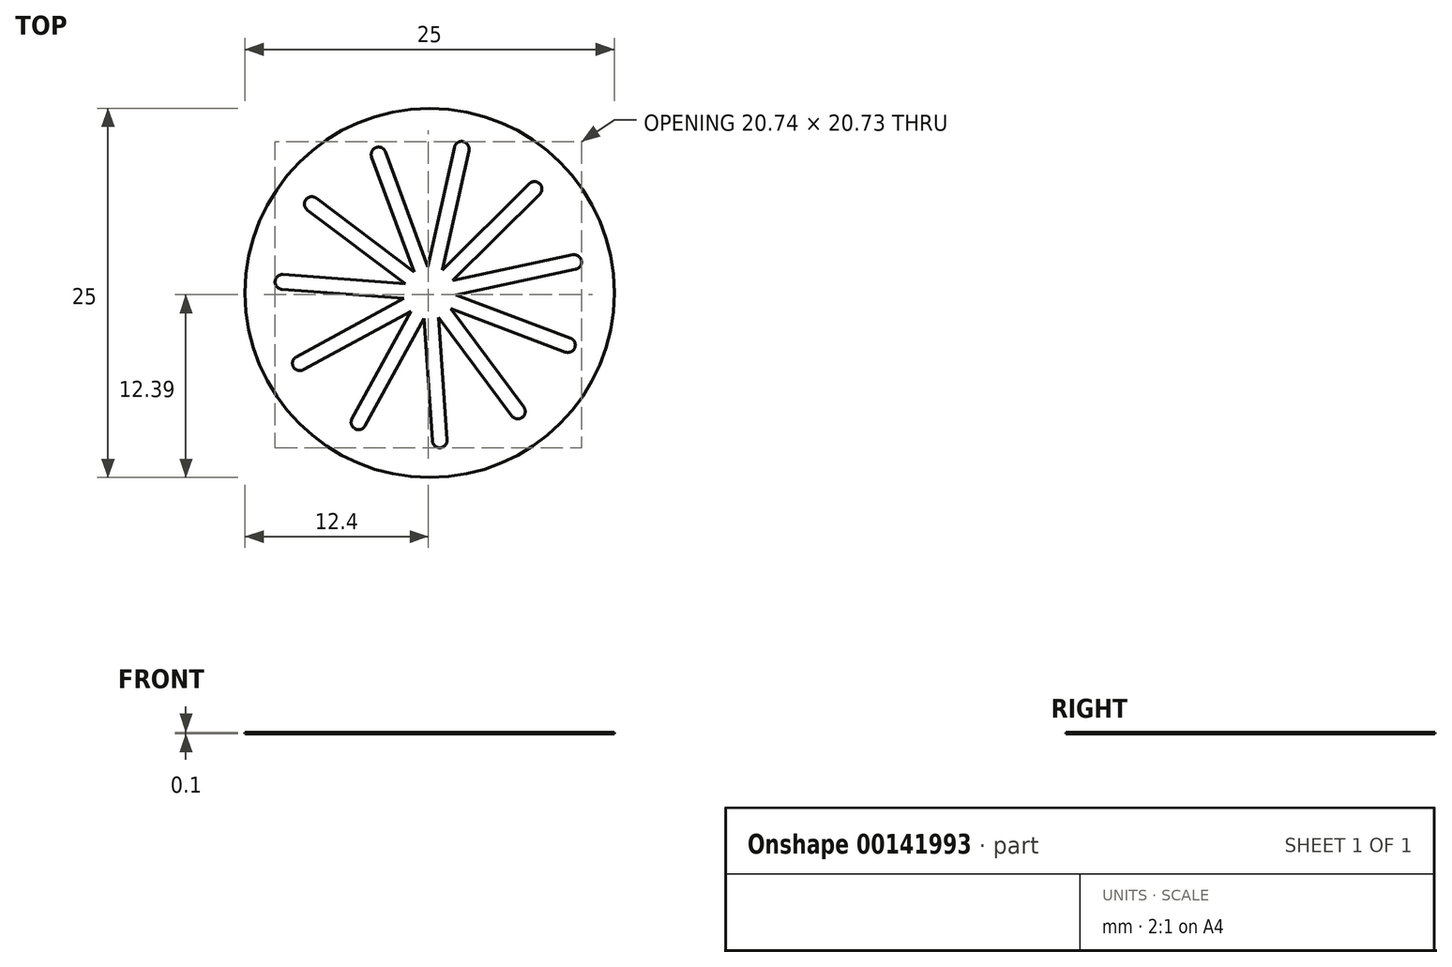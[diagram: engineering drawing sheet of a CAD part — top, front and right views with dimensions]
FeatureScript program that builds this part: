
annotation { "Feature Type Name" : "Feature", "Feature Type Description" : "" }
export const myFeature = defineFeature(function(context is Context, id is Id, definition is map)
    precondition{}
    {
        {
            var Q0;
            Q0=qCreatedBy(makeId("Top.planeOp"),FACE);
            var sketch = newSketch(context, id + "F0", { "sketchPlane" : qUnion([Q0])});
            skLineSegment(sketch, "E0", {"start": v(0.86, 1.55) * mm, "end": v(2.65, 9.66) * mm});
            skLineSegment(sketch, "E1", {"start": v(-0.12, 1.77) * mm, "end": v(1.67, 9.87) * mm});
            skArc(sketch, "E2", {"start": v(2.65, 9.66) * mm, "mid": v(2.27, 10.25) * mm, "end": v(1.67, 9.87) * mm});
            skArc(sketch, "E3.1.0", {"start": v(-3, 9.55) * mm, "mid": v(-3.63, 9.85) * mm, "end": v(-3.93, 9.2) * mm});
            skLineSegment(sketch, "E3.1.1", {"start": v(-0.12, 1.77) * mm, "end": v(-3, 9.55) * mm});
            skLineSegment(sketch, "E3.1.2", {"start": v(-1.06, 1.42) * mm, "end": v(-3.93, 9.2) * mm});
            skArc(sketch, "E3.2.0", {"start": v(-7.68, 6.42) * mm, "mid": v(-8.38, 6.32) * mm, "end": v(-8.29, 5.62) * mm});
            skLineSegment(sketch, "E3.2.1", {"start": v(-1.06, 1.42) * mm, "end": v(-7.68, 6.42) * mm});
            skLineSegment(sketch, "E3.2.2", {"start": v(-1.66, 0.63) * mm, "end": v(-8.29, 5.62) * mm});
            skArc(sketch, "E3.3.0", {"start": v(-9.93, 1.25) * mm, "mid": v(-10.47, 0.79) * mm, "end": v(-10, 0.25) * mm});
            skLineSegment(sketch, "E3.3.1", {"start": v(-1.66, 0.63) * mm, "end": v(-9.93, 1.25) * mm});
            skLineSegment(sketch, "E3.3.2", {"start": v(-1.74, -0.37) * mm, "end": v(-10, 0.25) * mm});
            skArc(sketch, "E3.4.0", {"start": v(-9.03, -4.32) * mm, "mid": v(-9.23, -5) * mm, "end": v(-8.56, -5.2) * mm});
            skLineSegment(sketch, "E3.4.1", {"start": v(-1.74, -0.37) * mm, "end": v(-9.03, -4.32) * mm});
            skLineSegment(sketch, "E3.4.2", {"start": v(-1.26, -1.25) * mm, "end": v(-8.56, -5.2) * mm});
            skArc(sketch, "E3.5.0", {"start": v(-5.26, -8.52) * mm, "mid": v(-5.06, -9.2) * mm, "end": v(-4.39, -9) * mm});
            skLineSegment(sketch, "E3.5.1", {"start": v(-1.26, -1.25) * mm, "end": v(-5.26, -8.52) * mm});
            skLineSegment(sketch, "E3.5.2", {"start": v(-0.38, -1.73) * mm, "end": v(-4.39, -9) * mm});
            skArc(sketch, "E3.6.0", {"start": v(0.18, -10.01) * mm, "mid": v(0.71, -10.48) * mm, "end": v(1.18, -9.94) * mm});
            skLineSegment(sketch, "E3.6.1", {"start": v(-0.38, -1.73) * mm, "end": v(0.18, -10.01) * mm});
            skLineSegment(sketch, "E3.6.2", {"start": v(0.61, -1.67) * mm, "end": v(1.18, -9.94) * mm});
            skArc(sketch, "E3.7.0", {"start": v(5.56, -8.32) * mm, "mid": v(6.26, -8.43) * mm, "end": v(6.37, -7.73) * mm});
            skLineSegment(sketch, "E3.7.1", {"start": v(0.61, -1.67) * mm, "end": v(5.56, -8.32) * mm});
            skLineSegment(sketch, "E3.7.2", {"start": v(1.42, -1.07) * mm, "end": v(6.37, -7.73) * mm});
            skArc(sketch, "E3.8.0", {"start": v(9.18, -4) * mm, "mid": v(9.82, -3.7) * mm, "end": v(9.53, -3.06) * mm});
            skLineSegment(sketch, "E3.8.1", {"start": v(1.42, -1.07) * mm, "end": v(9.18, -4) * mm});
            skLineSegment(sketch, "E3.8.2", {"start": v(1.77, -0.13) * mm, "end": v(9.53, -3.06) * mm});
            skArc(sketch, "E3.9.0", {"start": v(9.88, 1.6) * mm, "mid": v(10.27, 2.2) * mm, "end": v(9.67, 2.58) * mm});
            skLineSegment(sketch, "E3.9.1", {"start": v(1.77, -0.13) * mm, "end": v(9.88, 1.6) * mm});
            skLineSegment(sketch, "E3.9.2", {"start": v(1.56, 0.85) * mm, "end": v(9.67, 2.58) * mm});
            skArc(sketch, "E3.10.0", {"start": v(7.45, 6.7) * mm, "mid": v(7.45, 7.4) * mm, "end": v(6.74, 7.4) * mm});
            skLineSegment(sketch, "E3.10.1", {"start": v(1.56, 0.85) * mm, "end": v(7.45, 6.7) * mm});
            skLineSegment(sketch, "E3.10.2", {"start": v(0.86, 1.55) * mm, "end": v(6.74, 7.4) * mm});
            skPoint(sketch, "E3.center", {"position": v(0, 0) * mm});
            skCircle(sketch, "E4", {"center": v(0, 0) * mm, "radius": 12.5 * mm});
            skSolve(sketch);
        }
        {
            var Q0;
            Q0=makeQuery(id+"F0.imprint","IMPRINT",FACE,{"disambiguationData":[TD([[makeQuery(id+"F0.imprint","IMPRINT",EDGE,{"derivedFrom":sQuery(id+"F0.wireOp",EDGE,"E0")}),-1.0]])]});
            extrude(context, id + "F1", {"entities" : qUnion([Q0]), "depth" : 0.1 * mm});
        }
    });
